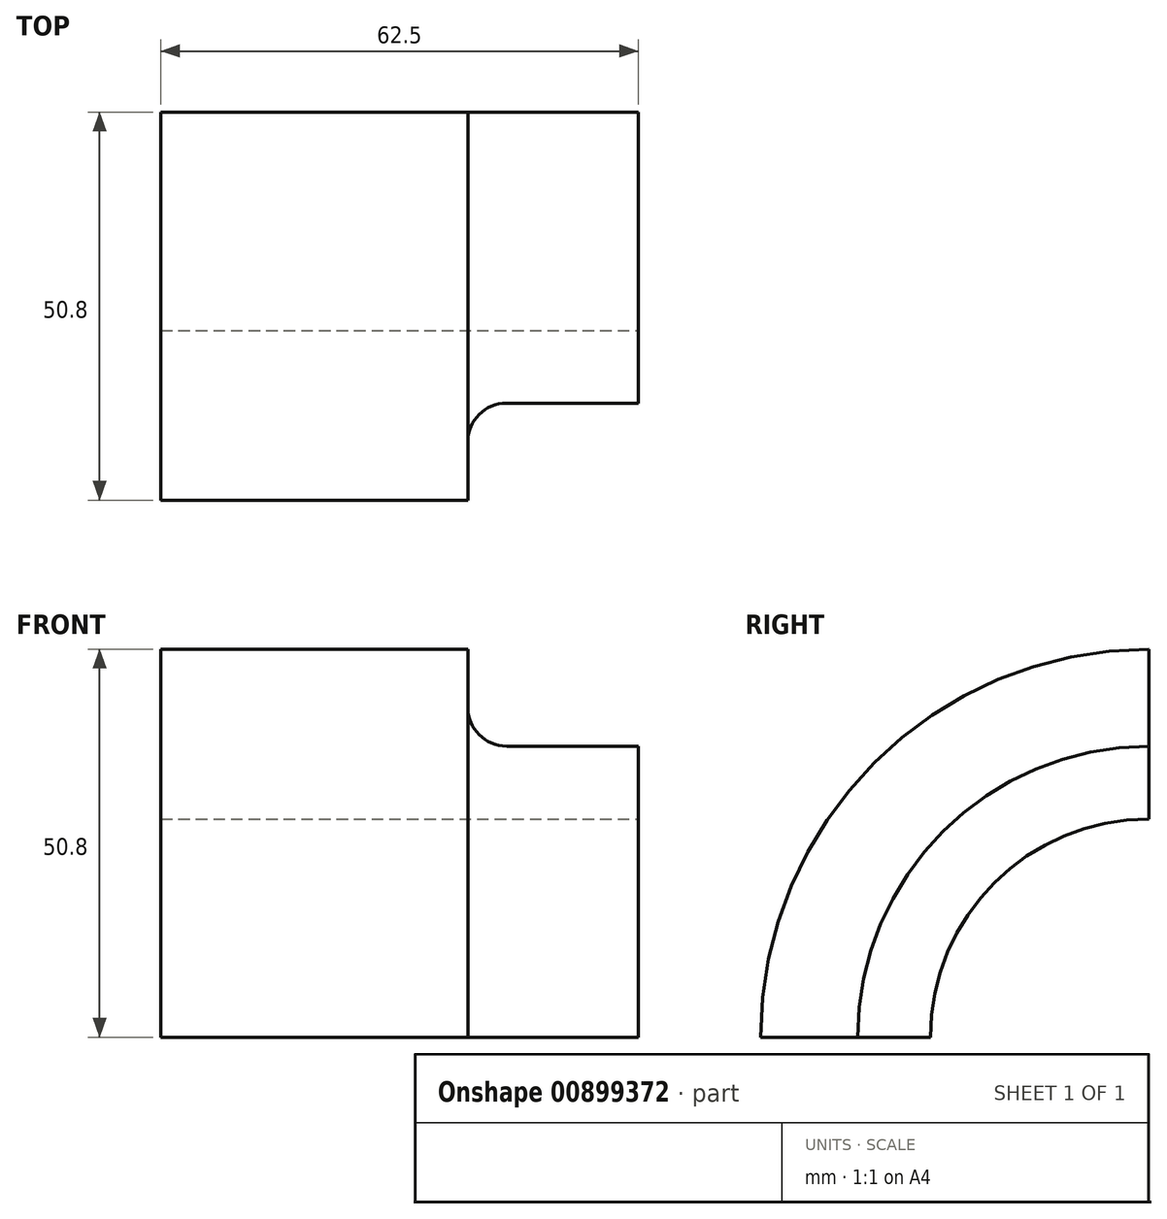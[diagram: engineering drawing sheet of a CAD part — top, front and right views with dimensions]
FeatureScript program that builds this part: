
annotation { "Feature Type Name" : "Feature", "Feature Type Description" : "" }
export const myFeature = defineFeature(function(context is Context, id is Id, definition is map)
    precondition{}
    {
        {
            var Q0;
            Q0=qCreatedBy(makeId("Front.planeOp"),FACE);
            var sketch = newSketch(context, id + "F0", { "sketchPlane" : qUnion([Q0])});
            skLineSegment(sketch, "E0", {"start": v(0, 0) * mm, "end": v(78.54, 0) * mm});
            skLineSegment(sketch, "E1", {"start": v(5.72, 50.8) * mm, "end": v(5.72, 28.58) * mm});
            skLineSegment(sketch, "E2", {"start": v(5.72, 28.58) * mm, "end": v(68.22, 28.58) * mm});
            skLineSegment(sketch, "E3", {"start": v(68.22, 28.58) * mm, "end": v(68.22, 38.1) * mm});
            skLineSegment(sketch, "E4", {"start": v(68.22, 38.1) * mm, "end": v(45.9, 38.1) * mm});
            skLineSegment(sketch, "E5", {"start": v(45.9, 38.1) * mm, "end": v(45.9, 50.8) * mm});
            skLineSegment(sketch, "E6", {"start": v(45.9, 50.8) * mm, "end": v(5.72, 50.8) * mm});
            skSolve(sketch);
        }
        {
            var Q0;
            Q0=makeQuery(id+"F0.imprint","IMPRINT",FACE,{"disambiguationData":[TD([[makeQuery(id+"F0.imprint","IMPRINT",EDGE,{"derivedFrom":sQuery(id+"F0.wireOp",EDGE,"E1")}),1.0]])]});
            var Q1;
            Q1=sQuery(id+"F0.wireOp",EDGE,"E0");
            revolve(context, id + "F1", {"surfaceOperationType" : NewSurfaceOperationType.NEW, "entities" : qUnion([Q0]), "axis" : qUnion([Q1]), "revolveType" : RevolveType.ONE_DIRECTION, "angle" : 90 * degree});
        }
        {
            var Q0;
            Q0=makeQuery(id+"F1.opRevolve","SWEPT_EDGE",EDGE,{"disambiguationData":[OSD([sQuery(id+"F0.wireOp",EDGE,"E4"),sQuery(id+"F0.wireOp",EDGE,"E5")])]});
            fillet(context, id + "F2", {"entities" : qUnion([Q0]), "radius" : 5.08 * mm, "tangentPropagation" : true, "allowEdgeOverflow" : false});
        }
    });
